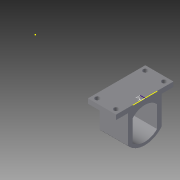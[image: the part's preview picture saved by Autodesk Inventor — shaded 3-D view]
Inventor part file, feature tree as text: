
AUTODESK INVENTOR PART (.ipt)
format: ipt  version: 2015 (Build 190159000, 159)  size: 285,696 bytes
history: native  units: in
note: dims shown in document units (in); Inventor stores cm internally (conversion verified against a paired STEP export)
features: sketch x22, extrude x20, fillet x2, plane x1, pattern_circular x1, mirror x1
ambient origin geometry x8: Origin, YZ Plane, XZ Plane, XY Plane, X Axis, Y Axis, Z Axis, Center Point
bodies: Solid1 (feature_tree)
feature tree (47):
  extrude  "Extrusion1"  Depth=0.1181in
  fillet  "Fillet1"  Radius=0.1969in
  fillet  "Fillet2"  [1 undecoded]
  plane  "Work Plane1"
  extrude  "Extrusion3"  Depth=0.1181in
  pattern_circular  "Circular Pattern1"  Count=4 Angle=360.0deg
  extrude  "Extrusion5"  Depth=0.1181in TaperAngle=0.0deg
  extrude  "Extrusion6"  Depth=0.1181in TaperAngle=0.0deg
  extrude  "Extrusion7"  Depth=0.3937in TaperAngle=0.0deg
  sketch  "Sketch11"  dims[d39=0.1969in d40=0.1181in d41=0.0in]
  extrude  "Extrusion8"  Depth=3.937in TaperAngle=0.0deg
  extrude  "Extrusion9"  Depth=0.1181in TaperAngle=0.0deg
  extrude  "Extrusion10"  Depth=0.5512in
  extrude  "Extrusion11"  Depth=0.7087in
  extrude  "Extrusion12"  Depth=0.3937in
  extrude  "Extrusion13"  Depth=0.1181in TaperAngle=0.0deg
  extrude  "Extrusion14"  Depth=0.0106in TaperAngle=0.0deg
  extrude  "Extrusion16"  Depth=0.1181in TaperAngle=0.0deg
  extrude  "Extrusion17"  Depth=0.2953in
  extrude  "Extrusion18"  Depth=0.1181in
  extrude  "Extrusion19"  Depth=0.1181in
  extrude  "Extrusion21"  Depth=0.1181in
  extrude  "Extrusion22"  Depth=0.2953in TaperAngle=0.0deg
  extrude  "Extrusion23"  [1 undecoded]
  extrude  "Extrusion24"  [1 undecoded]
  mirror  "Mirror1"
  sketch  "Sketch36"
  sketch  "Sketch1"  dims[d4=0.1181in d5=0.0in d6=0.1969in d7=0.1969in d8=-0.1969in]
  sketch  "Sketch6"  dims[d17=0.7087in d21=0.1181in]
  sketch  "Sketch8"  dims[d22=0.1181in]
  sketch  "Sketch9"  dims[d24=0.7087in d25=0.0in d26=1.5748in d27=360.0deg]
  sketch  "Sketch10"  dims[d35=0.1969in d36=0.1181in d37=0.0in]
  sketch  "Sketch12"  dims[d42=0.3937in d43=0.0in d44=3.937in d45=0.0in]
  sketch  "Sketch13"  dims[d46=3.937in d47=0.0in d48=3.937in d49=0.0in]
  sketch  "Sketch14"  dims[d50=0.1181in d51=3.937in d52=0.0in]
  sketch  "Sketch17"  dims[d53=0.5118in d54=0.0in d55=0.5512in]
  sketch  "Sketch18"  dims[d56=0.126in d57=0.7087in]
  sketch  "Sketch20"  dims[d58=0.3937in d59=0.3937in]
  sketch  "Sketch22"  dims[d60=0.7087in d61=0.0in d62=0.1181in d63=0.0in]
  sketch  "Sketch24"  dims[d69=0.0118in d70=0.0in d71=0.0106in d72=0.0in]
  sketch  "Sketch25"  dims[d73=0.0012in d74=0.0in d75=0.1181in d76=0.0in]
  sketch  "Sketch26"  dims[d84=1.1811in d85=0.0in d86=0.2953in]
  sketch  "Sketch27"  dims[d87=0.7087in d88=0.0in d89=0.1181in]
  sketch  "Sketch32"  dims[d90=0.1181in d91=0.1181in]
  sketch  "Sketch33"  dims[d92=0.1181in d93=0.1181in]
  sketch  "Sketch34"  dims[d94=0.7087in d95=0.0in d96=0.2953in d97=0.0in]
  sketch  "Sketch35"  dims[d98=0.1181in]
note: 3 required parameter values undecoded (feature->parameter linkage not recoverable at this tier; creation-order binding heuristic only, values carry confidence <= 0.55)
